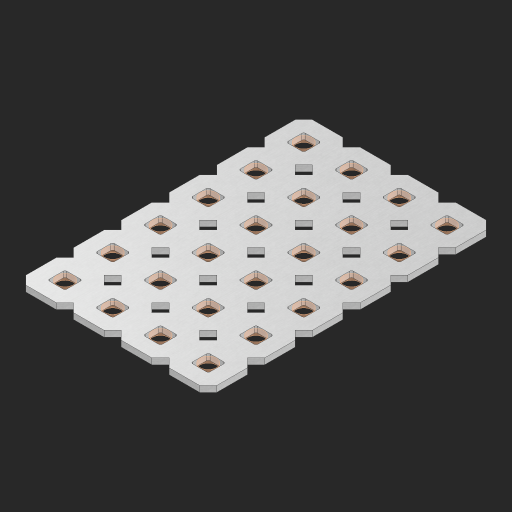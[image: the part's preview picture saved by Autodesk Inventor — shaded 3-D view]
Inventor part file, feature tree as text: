
AUTODESK INVENTOR PART (.ipt)
format: ipt  version: 2023 (Build 270158000, 158)  size: 579,584 bytes
history: native  units: in
note: dims shown in document units (in); Inventor stores cm internally (conversion verified against a paired STEP export)
features: other x25, extrude x23, sketch x2, pattern_linear x1
ambient origin geometry x8: Origin, YZ Plane, XZ Plane, XY Plane, X Axis, Y Axis, Z Axis, Center Point
bodies: Solid1 (feature_tree), Body (feature_tree)
feature tree (51):
  pattern_linear  "Rectangular Pattern1"  Spacing1=0.09in  [1 undecoded]
  sketch  "Sketch1"  dims[d1=0.5in]
  sketch  "Sketch2"  dims[d2=0.182in d3=0.09in d4=0.09in d5=0.09in d6=0.09in d7=0.09in d8=0.09in d9=0.09in d10=0.09in d11=0.02in d13=0.0in d14=0.172in d15=0.0625in d16=0.0in d19=0.5in d22=0.5in]
  other  "Srf1"
  other  "Srf126"
  other  "Srf127"
  other  "Srf128"
  other  "Srf129"
  other  "Srf130"
  other  "Srf268"
  other  "Srf269"
  other  "Srf270"
  other  "Srf271"
  other  "Srf272"
  other  "Srf273"
  other  "Srf293"
  other  "Srf294"
  other  "Srf295"
  other  "Srf296"
  other  "Srf297"
  other  "Srf298"
  other  "Srf318"
  other  "Srf319"
  other  "Srf320"
  other  "Srf321"
  other  "Srf322"
  other  "Srf323"
  other  "Circle"
  extrude  "ExtrusionSrf126"  Depth=0.09in
  extrude  "ExtrusionSrf127"  Depth=0.09in
  extrude  "ExtrusionSrf128"  Depth=0.09in
  extrude  "ExtrusionSrf129"  Depth=0.09in
  extrude  "ExtrusionSrf130"  Depth=0.09in
  extrude  "ExtrusionSrf268"  Depth=0.09in
  extrude  "ExtrusionSrf269"  Depth=0.09in
  extrude  "ExtrusionSrf270"  Depth=0.02in
  extrude  "ExtrusionSrf271"  TaperAngle=0.0deg  [1 undecoded]
  extrude  "ExtrusionSrf272"  Depth=0.5in
  extrude  "ExtrusionSrf273"  Depth=0.0625in TaperAngle=0.0deg
  extrude  "ExtrusionSrf293"  Depth=0.5in
  extrude  "ExtrusionSrf294"  Depth=0.5in
  extrude  "ExtrusionSrf295"  [1 undecoded]
  extrude  "ExtrusionSrf296"  [1 undecoded]
  extrude  "ExtrusionSrf297"  [1 undecoded]
  extrude  "ExtrusionSrf298"  [1 undecoded]
  extrude  "ExtrusionSrf318"  [1 undecoded]
  extrude  "ExtrusionSrf319"  [1 undecoded]
  extrude  "ExtrusionSrf320"  [1 undecoded]
  extrude  "ExtrusionSrf321"  [1 undecoded]
  extrude  "ExtrusionSrf322"  [1 undecoded]
  extrude  "ExtrusionSrf323"  [1 undecoded]
note: 12 required parameter values undecoded (feature->parameter linkage not recoverable at this tier; creation-order binding heuristic only, values carry confidence <= 0.55)
